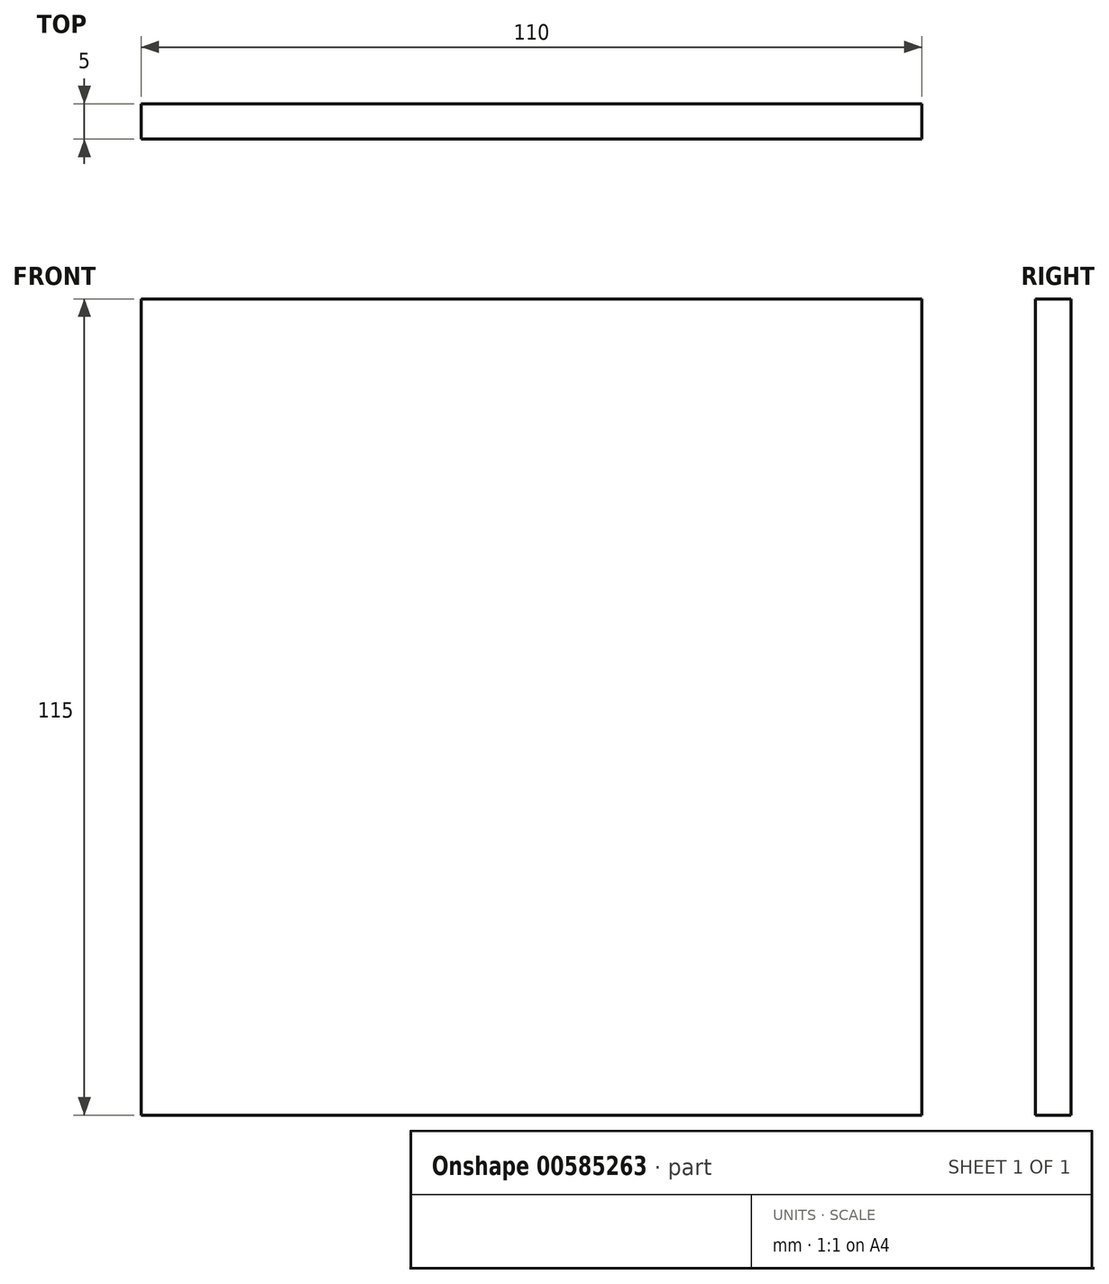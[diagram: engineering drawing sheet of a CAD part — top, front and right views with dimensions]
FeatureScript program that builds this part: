
annotation { "Feature Type Name" : "Feature", "Feature Type Description" : "" }
export const myFeature = defineFeature(function(context is Context, id is Id, definition is map)
    precondition{}
    {
        {
            var Q0;
            Q0=qCreatedBy(makeId("Front.planeOp"),FACE);
            var sketch = newSketch(context, id + "F0", { "sketchPlane" : qUnion([Q0])});
            skLineSegment(sketch, "E0", {"start": v(-75.2, 72.73) * mm, "end": v(34.8, 72.73) * mm});
            skLineSegment(sketch, "E1", {"start": v(34.8, 72.73) * mm, "end": v(34.8, -42.27) * mm});
            skLineSegment(sketch, "E2", {"start": v(34.8, -42.27) * mm, "end": v(-75.2, -42.27) * mm});
            skLineSegment(sketch, "E3", {"start": v(-75.2, -42.27) * mm, "end": v(-75.2, 72.73) * mm});
            skSolve(sketch);
        }
        {
            var Q0;
            Q0=makeQuery(id+"F0.imprint","IMPRINT",FACE,{"disambiguationData":[TD([[makeQuery(id+"F0.imprint","IMPRINT",EDGE,{"derivedFrom":sQuery(id+"F0.wireOp",EDGE,"E0")}),-1.0]])]});
            extrude(context, id + "F1", {"entities" : qUnion([Q0]), "depth" : 5 * mm, "offsetDistance" : 25 * mm});
        }
    });
